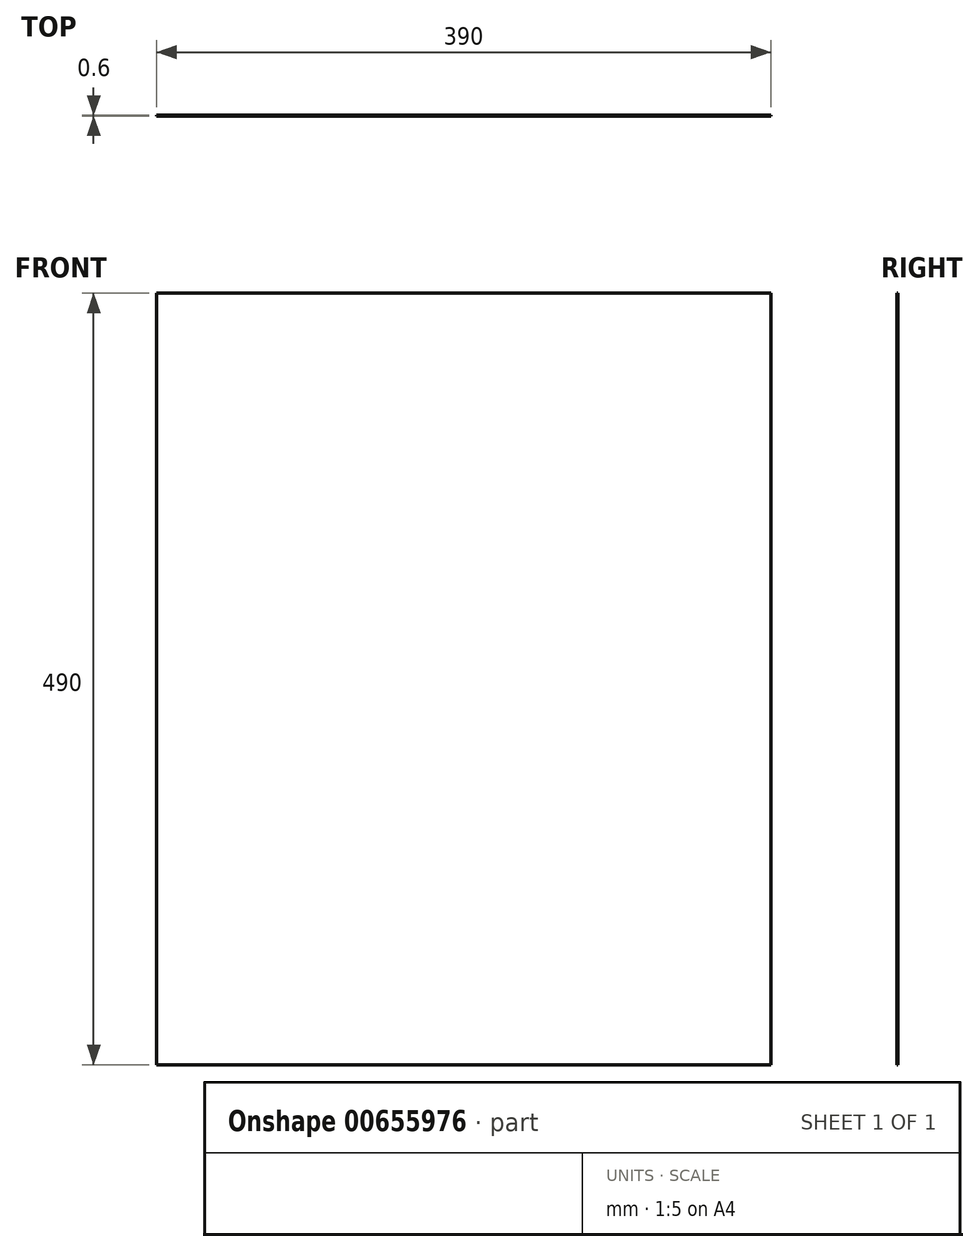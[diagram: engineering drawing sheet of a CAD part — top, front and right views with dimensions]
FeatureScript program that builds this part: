
annotation { "Feature Type Name" : "Feature", "Feature Type Description" : "" }
export const myFeature = defineFeature(function(context is Context, id is Id, definition is map)
    precondition{}
    {
        {
            var Q0;
            Q0=qCreatedBy(makeId("Front.planeOp"),FACE);
            var sketch = newSketch(context, id + "F0", { "sketchPlane" : qUnion([Q0])});
            skLineSegment(sketch, "E0.bottom", {"start": v(0, 0) * mm, "end": v(390, 0) * mm});
            skLineSegment(sketch, "E0.top", {"start": v(0, 490) * mm, "end": v(390, 490) * mm});
            skLineSegment(sketch, "E0.left", {"start": v(0, 0) * mm, "end": v(0, 490) * mm});
            skLineSegment(sketch, "E0.right", {"start": v(390, 0) * mm, "end": v(390, 490) * mm});
            skSolve(sketch);
        }
        {
            var Q0;
            Q0=makeQuery(id+"F0.imprint","IMPRINT",FACE,{"disambiguationData":[TD([[makeQuery(id+"F0.imprint","IMPRINT",EDGE,{"derivedFrom":sQuery(id+"F0.wireOp",EDGE,"E0.bottom")}),1.0]])]});
            extrude(context, id + "F1", {"entities" : qUnion([Q0]), "depth" : 0.6 * mm, "offsetDistance" : 25.4 * mm});
        }
    });
